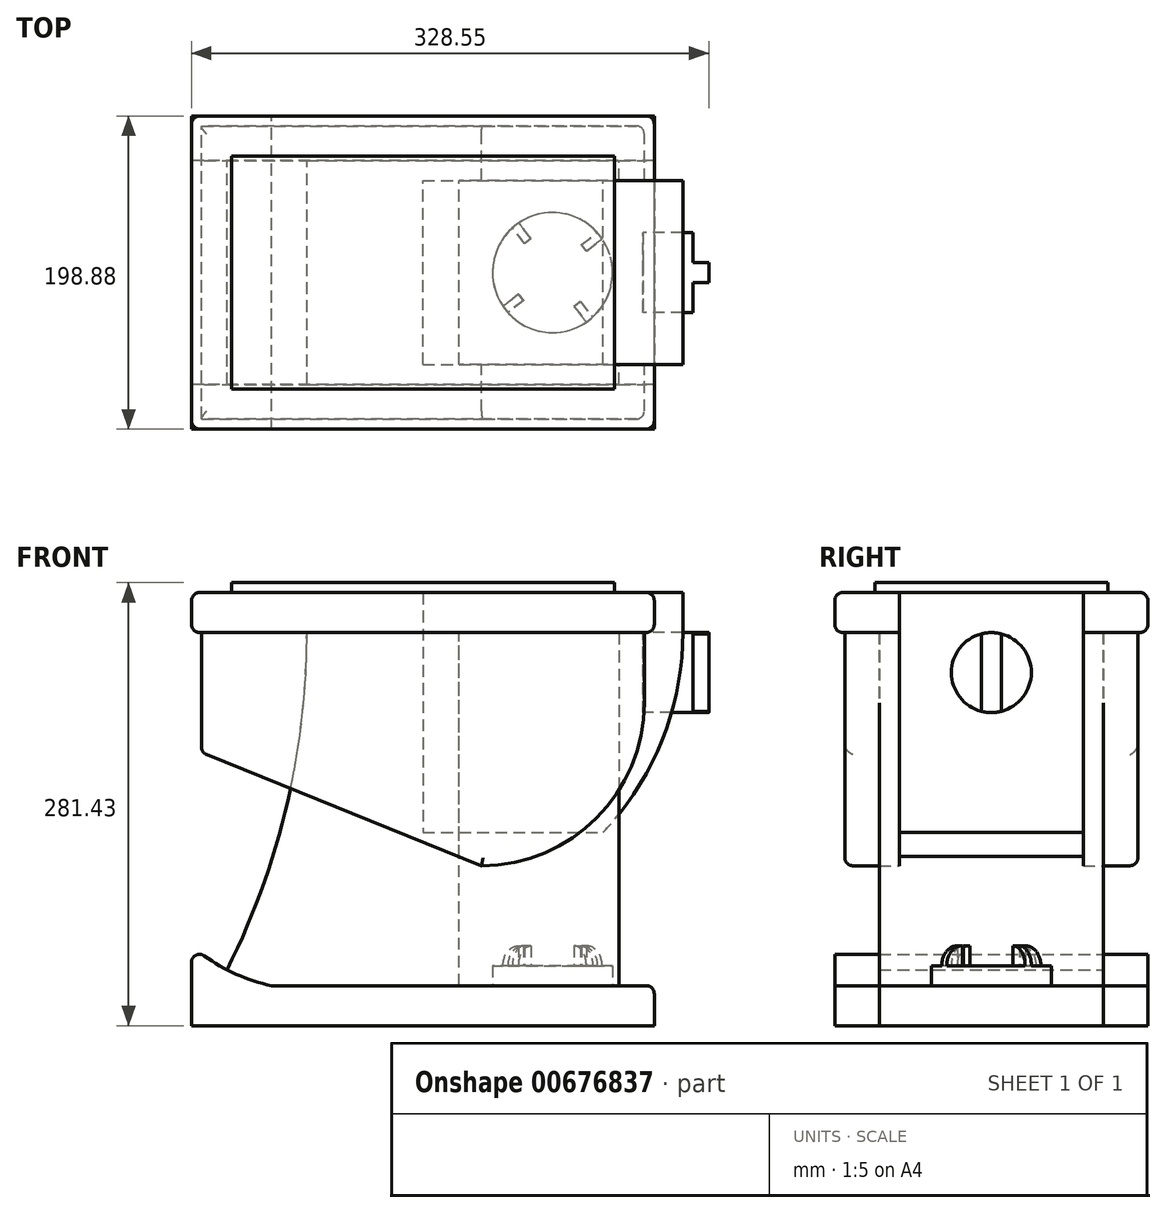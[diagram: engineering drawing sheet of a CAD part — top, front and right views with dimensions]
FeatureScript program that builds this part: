
annotation { "Feature Type Name" : "Feature", "Feature Type Description" : "" }
export const myFeature = defineFeature(function(context is Context, id is Id, definition is map)
    precondition{}
    {
        {
            var Q0;
            Q0=qCreatedBy(makeId("Top.planeOp"),FACE);
            var sketch = newSketch(context, id + "F0", { "sketchPlane" : qUnion([Q0])});
            skLineSegment(sketch, "E0.top", {"start": v(0, 99.44) * mm, "end": v(146.94, 99.44) * mm});
            skLineSegment(sketch, "E0.right", {"start": v(146.94, 0) * mm, "end": v(146.94, 99.44) * mm});
            skLineSegment(sketch, "E1.MirrorCS", {"start": v(0, 99.44) * mm, "end": v(-146.94, 99.44) * mm});
            skLineSegment(sketch, "E2.MirrorCS", {"start": v(-146.94, 0) * mm, "end": v(-146.94, 99.44) * mm});
            skLineSegment(sketch, "E3.MirrorCS", {"start": v(0, -99.44) * mm, "end": v(146.94, -99.44) * mm});
            skLineSegment(sketch, "E4.MirrorCS", {"start": v(146.94, 0) * mm, "end": v(146.94, -99.44) * mm});
            skLineSegment(sketch, "E5.MirrorCS", {"start": v(-146.94, 0) * mm, "end": v(-146.94, -99.44) * mm});
            skLineSegment(sketch, "E6.MirrorCS", {"start": v(0, -99.44) * mm, "end": v(-146.94, -99.44) * mm});
            skSolve(sketch);
        }
        {
            var Q0;
            Q0=qSketchRegion(id+"F0",true);
            extrude(context, id + "F1", {"entities" : qUnion([Q0]), "depth" : 25.4 * mm, "offsetDistance" : 25.4 * mm});
        }
        {
            var Q0;
            Q0=qCreatedBy(makeId("Front.planeOp"),FACE);
            var sketch = newSketch(context, id + "F2", { "sketchPlane" : qUnion([Q0])});
            skLineSegment(sketch, "E7.bottom", {"start": v(0, 0) * mm, "end": v(-140.59, 0) * mm});
            skLineSegment(sketch, "E7.top", {"start": v(0, -76.2) * mm, "end": v(-140.59, -76.2) * mm});
            skLineSegment(sketch, "E7.left", {"start": v(0, 0) * mm, "end": v(0, -76.2) * mm});
            skLineSegment(sketch, "E7.right", {"start": v(-140.59, 0) * mm, "end": v(-140.59, -76.2) * mm});
            skLineSegment(sketch, "E8.0", {"start": v(37.21, -148.08) * mm, "end": v(140.59, -148.08) * mm});
            skLineSegment(sketch, "E9", {"start": v(-140.59, -76.2) * mm, "end": v(37.21, -148.08) * mm});
            skLineSegment(sketch, "E10.0", {"start": v(140.59, 0) * mm, "end": v(140.59, -148.08) * mm});
            skLineSegment(sketch, "E11", {"start": v(0, 0) * mm, "end": v(140.59, 0) * mm});
            skSolve(sketch);
        }
        {
            var Q0;
            Q0=qSketchRegion(id+"F2",true);
            extrude(context, id + "F3", {"entities" : qUnion([Q0]), "operationType" : NewBodyOperationType.ADD, "depth" : 93.1 * mm, "offsetDistance" : 25.4 * mm, "hasSecondDirection" : true, "secondDirectionOppositeDirection" : true, "secondDirectionDepth" : 93.1 * mm});
        }
        {
            var Q0;
            Q0=qCreatedBy(makeId("Front.planeOp"),FACE);
            var sketch = newSketch(context, id + "F4", { "sketchPlane" : qUnion([Q0])});
            skLineSegment(sketch, "E12.bottom", {"start": v(0, 0) * mm, "end": v(124.46, 0) * mm});
            skLineSegment(sketch, "E12.top", {"start": v(0, -224.28) * mm, "end": v(124.46, -224.28) * mm});
            skLineSegment(sketch, "E12.left", {"start": v(0, 0) * mm, "end": v(0, -224.28) * mm});
            skLineSegment(sketch, "E12.right", {"start": v(124.46, 0) * mm, "end": v(124.46, -224.28) * mm});
            skLineSegment(sketch, "E13.MirrorCS", {"start": v(0, -224.28) * mm, "end": v(-96.14, -224.28) * mm});
            skLineSegment(sketch, "E14.bottom", {"start": v(0, -224.28) * mm, "end": v(146.94, -224.28) * mm});
            skLineSegment(sketch, "E14.top", {"start": v(0, -249.68) * mm, "end": v(146.94, -249.68) * mm});
            skLineSegment(sketch, "E14.right", {"start": v(146.94, -224.28) * mm, "end": v(146.94, -249.68) * mm});
            skLineSegment(sketch, "E15.MirrorCS", {"start": v(0, -249.68) * mm, "end": v(-146.94, -249.68) * mm});
            skLineSegment(sketch, "E16.MirrorCS", {"start": v(-146.94, -198.88) * mm, "end": v(-146.94, -249.68) * mm});
            skPoint(sketch, "E17.orphan", {"position": v(-146.94, -224.28) * mm});
            skArc(sketch, "E18", {"start": v(-146.94, -198.88) * mm, "mid": v(-123.18, -214.86) * mm, "end": v(-96.14, -224.28) * mm});
            skPoint(sketch, "E19.orphan", {"position": v(-124.46, -224.28) * mm});
            skLineSegment(sketch, "E20", {"start": v(-124.46, 0) * mm, "end": v(0, 0) * mm});
            skArc(sketch, "E21", {"start": v(-124.46, -214.2) * mm, "mid": v(-86.53, -110.07) * mm, "end": v(-73.66, 0) * mm});
            skSolve(sketch);
        }
        {
            var Q0;
            Q0=makeQuery(id+"F4.imprint","IMPRINT",FACE,{"disambiguationData":[TD([[makeQuery(id+"F4.imprint","IMPRINT",EDGE,{"derivedFrom":sQuery(id+"F4.wireOp",EDGE,"E14.top")}),1.0]])]});
            extrude(context, id + "F5", {"entities" : qUnion([Q0]), "depth" : 99.44 * mm, "offsetDistance" : 25.4 * mm, "hasSecondDirection" : true, "secondDirectionOppositeDirection" : true, "secondDirectionDepth" : 99.44 * mm});
        }
        {
            var Q0;
            Q0=qSketchRegion(id+"F4",true);
            extrude(context, id + "F6", {"entities" : qUnion([Q0]), "depth" : 71.12 * mm, "offsetDistance" : 25.4 * mm, "hasSecondDirection" : true, "secondDirectionOppositeDirection" : true, "secondDirectionDepth" : 71.12 * mm});
        }
        {
            var Q0;
            Q0=makeQuery(id+"F3.opExtrude","SWEPT_EDGE",EDGE,{"disambiguationData":[OSD([sQuery(id+"F2.wireOp",EDGE,"E8.0"),sQuery(id+"F2.wireOp",EDGE,"E10.0")])]});
            fillet(context, id + "F7", {"entities" : qUnion([Q0]), "radius" : 103.38 * mm, "tangentPropagation" : true, "allowEdgeOverflow" : false});
        }
        {
            var Q0;
            Q0=makeQuery(id+"F6.opExtrude","SWEPT_FACE",FACE,{"disambiguationData":[OSD([sQuery(id+"F4.wireOp",EDGE,"E12.right")])]});
            var sketch = newSketch(context, id + "F8", { "sketchPlane" : qUnion([Q0])});
            skLineSegment(sketch, "E22.0", {"start": v(-58.42, -224.28) * mm, "end": v(-58.42, -49.7) * mm});
            skLineSegment(sketch, "E23.bottom", {"start": v(-58.42, -224.28) * mm, "end": v(58.42, -224.28) * mm});
            skLineSegment(sketch, "E23.top", {"start": v(-58.42, 0) * mm, "end": v(58.42, 0) * mm});
            skLineSegment(sketch, "E23.left", {"start": v(-58.42, -224.28) * mm, "end": v(-58.42, 0) * mm});
            skLineSegment(sketch, "E23.right", {"start": v(58.42, -224.28) * mm, "end": v(58.42, 0) * mm});
            skSolve(sketch);
        }
        {
            var Q0;
            Q0=makeQuery(id+"F1.opExtrude","CAP_FACE",FACE,{"disambiguationData":[OSD([sQuery(id+"F0.wireOp",EDGE,"E0.top"),sQuery(id+"F0.wireOp",EDGE,"E0.right"),sQuery(id+"F0.wireOp",EDGE,"E1.MirrorCS"),sQuery(id+"F0.wireOp",EDGE,"E2.MirrorCS"),sQuery(id+"F0.wireOp",EDGE,"E3.MirrorCS"),sQuery(id+"F0.wireOp",EDGE,"E4.MirrorCS"),sQuery(id+"F0.wireOp",EDGE,"E5.MirrorCS"),sQuery(id+"F0.wireOp",EDGE,"E6.MirrorCS")])],"isStart":false});
            var Q1;
            Q1=makeQuery(id+"F1.opExtrude","CAP_EDGE",EDGE,{"disambiguationData":[OSD([sQuery(id+"F0.wireOp",EDGE,"E3.MirrorCS"),sQuery(id+"F0.wireOp",EDGE,"E6.MirrorCS")])],"isStart":true});
            var Q2;
            Q2=makeQuery(id+"F1.opExtrude","CAP_EDGE",EDGE,{"disambiguationData":[OSD([sQuery(id+"F0.wireOp",EDGE,"E2.MirrorCS"),sQuery(id+"F0.wireOp",EDGE,"E5.MirrorCS")])],"isStart":true});
            var Q3;
            Q3=makeQuery(id+"F1.opExtrude","SWEPT_FACE",FACE,{"disambiguationData":[OSD([sQuery(id+"F0.wireOp",EDGE,"E0.right"),sQuery(id+"F0.wireOp",EDGE,"E4.MirrorCS")])]});
            var Q4;
            Q4=makeQuery(id+"F1.opExtrude","SWEPT_FACE",FACE,{"disambiguationData":[OSD([sQuery(id+"F0.wireOp",EDGE,"E2.MirrorCS"),sQuery(id+"F0.wireOp",EDGE,"E5.MirrorCS")])]});
            var Q5;
            Q5=makeQuery(id+"F1.opExtrude","SWEPT_FACE",FACE,{"disambiguationData":[OSD([sQuery(id+"F0.wireOp",EDGE,"E0.top"),sQuery(id+"F0.wireOp",EDGE,"E1.MirrorCS")])]});
            fillet(context, id + "F9", {"entities" : qUnion([Q0, Q1, Q2, Q3, Q4, Q5]), "radius" : 5.08 * mm, "tangentPropagation" : true, "allowEdgeOverflow" : false});
        }
        {
            var Q0;
            Q0=makeQuery(id+"F3.opExtrude","SWEPT_EDGE",EDGE,{"disambiguationData":[OSD([sQuery(id+"F2.wireOp",EDGE,"E7.top"),sQuery(id+"F2.wireOp",EDGE,"E7.right"),sQuery(id+"F2.wireOp",EDGE,"E9")])]});
            var Q1;
            Q1=makeQuery(id+"F3.opExtrude","CAP_EDGE",EDGE,{"disambiguationData":[OSD([sQuery(id+"F2.wireOp",EDGE,"E9")])],"isStart":false});
            var Q2;
            Q2=makeQuery(id+"F3.opExtrude","CAP_EDGE",EDGE,{"disambiguationData":[OSD([sQuery(id+"F2.wireOp",EDGE,"E9")])],"isStart":true});
            var Q3;
            {var subQ0=sQuery(id+"F2.wireOp",EDGE,"E10.0");var subQ1=sQuery(id+"F2.wireOp",EDGE,"E8.0");Q3=makeQuery(id+"F7.opFillet","BLEND_EDGE",EDGE,{"blendedFrom":[makeQuery(id+"F3.opExtrude","SWEPT_EDGE",EDGE,{"disambiguationData":[OSD([subQ1,subQ0])]}),makeQuery(id+"F3.opExtrude","CAP_FACE",FACE,{"disambiguationData":[OSD([sQuery(id+"F2.wireOp",EDGE,"E7.bottom"),sQuery(id+"F2.wireOp",EDGE,"E7.right"),subQ1,sQuery(id+"F2.wireOp",EDGE,"E9"),subQ0,sQuery(id+"F2.wireOp",EDGE,"E11")])],"isStart":true})],"blendedInto":[makeQuery(id+"F3.opExtrude","CAP_FACE",FACE,{"disambiguationData":[OSD([sQuery(id+"F2.wireOp",EDGE,"E7.bottom"),sQuery(id+"F2.wireOp",EDGE,"E7.right"),subQ1,sQuery(id+"F2.wireOp",EDGE,"E9"),subQ0,sQuery(id+"F2.wireOp",EDGE,"E11")])],"isStart":true})]});}
            var Q4;
            {var subQ0=sQuery(id+"F2.wireOp",EDGE,"E10.0");var subQ1=sQuery(id+"F2.wireOp",EDGE,"E8.0");Q4=makeQuery(id+"F7.opFillet","BLEND_EDGE",EDGE,{"blendedFrom":[makeQuery(id+"F3.opExtrude","SWEPT_EDGE",EDGE,{"disambiguationData":[OSD([subQ1,subQ0])]}),makeQuery(id+"F3.opExtrude","CAP_FACE",FACE,{"disambiguationData":[OSD([sQuery(id+"F2.wireOp",EDGE,"E7.bottom"),sQuery(id+"F2.wireOp",EDGE,"E7.right"),subQ1,sQuery(id+"F2.wireOp",EDGE,"E9"),subQ0,sQuery(id+"F2.wireOp",EDGE,"E11")])],"isStart":false})],"blendedInto":[makeQuery(id+"F3.opExtrude","CAP_FACE",FACE,{"disambiguationData":[OSD([sQuery(id+"F2.wireOp",EDGE,"E7.bottom"),sQuery(id+"F2.wireOp",EDGE,"E7.right"),subQ1,sQuery(id+"F2.wireOp",EDGE,"E9"),subQ0,sQuery(id+"F2.wireOp",EDGE,"E11")])],"isStart":false})]});}
            var Q5;
            Q5=makeQuery(id+"F5.opExtrude","SWEPT_EDGE",EDGE,{"disambiguationData":[OSD([sQuery(id+"F4.wireOp",EDGE,"E16.MirrorCS"),sQuery(id+"F4.wireOp",EDGE,"E18")])]});
            var Q6;
            Q6=makeQuery(id+"F6.opExtrude","SWEPT_EDGE",EDGE,{"disambiguationData":[OSD([sQuery(id+"F4.wireOp",EDGE,"E16.MirrorCS"),sQuery(id+"F4.wireOp",EDGE,"E18")])]});
            var Q7;
            Q7=makeQuery(id+"F6.opExtrude","SWEPT_EDGE",EDGE,{"disambiguationData":[OSD([sQuery(id+"F4.wireOp",EDGE,"E14.bottom"),sQuery(id+"F4.wireOp",EDGE,"E14.right")])]});
            var Q8;
            Q8=makeQuery(id+"F5.opExtrude","SWEPT_EDGE",EDGE,{"disambiguationData":[OSD([sQuery(id+"F4.wireOp",EDGE,"E14.bottom"),sQuery(id+"F4.wireOp",EDGE,"E14.right")])]});
            fillet(context, id + "F10", {"entities" : qUnion([Q0, Q1, Q2, Q3, Q4, Q5, Q6, Q7, Q8]), "radius" : 5.08 * mm, "tangentPropagation" : true, "allowEdgeOverflow" : false});
        }
        {
            var Q0;
            Q0=makeQuery(id+"F1.opExtrude","CAP_FACE",FACE,{"disambiguationData":[OSD([sQuery(id+"F0.wireOp",EDGE,"E0.top"),sQuery(id+"F0.wireOp",EDGE,"E0.right"),sQuery(id+"F0.wireOp",EDGE,"E1.MirrorCS"),sQuery(id+"F0.wireOp",EDGE,"E2.MirrorCS"),sQuery(id+"F0.wireOp",EDGE,"E3.MirrorCS"),sQuery(id+"F0.wireOp",EDGE,"E4.MirrorCS"),sQuery(id+"F0.wireOp",EDGE,"E5.MirrorCS"),sQuery(id+"F0.wireOp",EDGE,"E6.MirrorCS")])],"isStart":false});
            var sketch = newSketch(context, id + "F11", { "sketchPlane" : qUnion([Q0])});
            skLineSegment(sketch, "E24.bottom", {"start": v(121.54, 74.04) * mm, "end": v(-121.54, 74.04) * mm});
            skLineSegment(sketch, "E24.top", {"start": v(121.54, -74.04) * mm, "end": v(-121.54, -74.04) * mm});
            skLineSegment(sketch, "E24.left", {"start": v(121.54, 74.04) * mm, "end": v(121.54, -74.04) * mm});
            skLineSegment(sketch, "E24.right", {"start": v(-121.54, 74.04) * mm, "end": v(-121.54, -74.04) * mm});
            skPoint(sketch, "E24.middle", {"position": v(0, 0) * mm});
            skSolve(sketch);
        }
        {
            var Q0;
            Q0=qSketchRegion(id+"F11",true);
            extrude(context, id + "F12", {"entities" : qUnion([Q0]), "operationType" : NewBodyOperationType.ADD, "depth" : 6.35 * mm, "offsetDistance" : 25.4 * mm});
        }
        {
            var Q0;
            {var subQ4=sQuery(id+"F8.wireOp",EDGE,"E23.bottom");Q0=makeQuery(id+"F8.imprint","IMPRINT",FACE,{"disambiguationData":[TD([[makeQuery(id+"F8.imprint","IMPRINT",EDGE,{"derivedFrom":subQ4}),1.0]])]});}
            extrude(context, id + "F13", {"entities" : qUnion([Q0]), "operationType" : NewBodyOperationType.REMOVE, "oppositeDirection" : true, "depth" : 101.6 * mm, "offsetDistance" : 25.4 * mm, "hasSecondDirection" : true, "secondDirectionOppositeDirection" : false, "secondDirectionDepth" : 25.4 * mm});
        }
        {
            var Q0;
            Q0=qCreatedBy(makeId("Front.planeOp"),FACE);
            var sketch = newSketch(context, id + "F14", { "sketchPlane" : qUnion([Q0])});
            skLineSegment(sketch, "E25.bottom", {"start": v(0, 0) * mm, "end": v(165.1, 0) * mm});
            skLineSegment(sketch, "E25.top", {"start": v(0, -127) * mm, "end": v(114.3, -127) * mm});
            skLineSegment(sketch, "E25.left", {"start": v(0, 0) * mm, "end": v(0, -127) * mm});
            skLineSegment(sketch, "E26.top", {"start": v(0, 25.4) * mm, "end": v(165.1, 25.4) * mm});
            skLineSegment(sketch, "E26.left", {"start": v(0, 0) * mm, "end": v(0, 25.4) * mm});
            skLineSegment(sketch, "E26.right", {"start": v(165.1, 0) * mm, "end": v(165.1, 25.4) * mm});
            skArc(sketch, "E27", {"start": v(114.3, -127) * mm, "mid": v(151.93, -68.4) * mm, "end": v(165.1, 0) * mm});
            skSolve(sketch);
        }
        {
            var Q0;
            Q0=qSketchRegion(id+"F14",true);
            extrude(context, id + "F15", {"entities" : qUnion([Q0]), "depth" : 58.42 * mm, "offsetDistance" : 25.4 * mm, "hasSecondDirection" : true, "secondDirectionOppositeDirection" : true, "secondDirectionDepth" : 58.42 * mm});
        }
        {
            var Q0;
            Q0=makeQuery(id+"F15.opExtrude","SWEPT_FACE",FACE,{"disambiguationData":[OSD([sQuery(id+"F14.wireOp",EDGE,"E26.right")])]});
            var sketch = newSketch(context, id + "F16", { "sketchPlane" : qUnion([Q0])});
            skLineSegment(sketch, "E28", {"start": v(0, 25.4) * mm, "end": v(0, -81.4) * mm});
            skLineSegment(sketch, "E29", {"start": v(0, 25.4) * mm, "end": v(34.21, 25.4) * mm});
            skLineSegment(sketch, "E30.0", {"start": v(0, -25.4) * mm, "end": v(34.21, -25.4) * mm});
            skCircle(sketch, "E31", {"center": v(0, -25.4) * mm, "radius": 25.4 * mm});
            skSolve(sketch);
        }
        {
            var Q0;
            Q0=qSketchRegion(id+"F16",true);
            extrude(context, id + "F17", {"entities" : qUnion([Q0]), "depth" : 6.35 * mm, "offsetDistance" : 25.4 * mm, "hasSecondDirection" : true, "secondDirectionOppositeDirection" : true, "secondDirectionDepth" : 25.4 * mm});
        }
        {
            var Q0;
            Q0=makeQuery(id+"F17.opExtrude","CAP_FACE",FACE,{"disambiguationData":[OSD([sQuery(id+"F16.wireOp",EDGE,"E31")])],"isStart":false});
            var sketch = newSketch(context, id + "F18", { "sketchPlane" : qUnion([Q0])});
            skArc(sketch, "E32", {"start": v(-6.35, -50) * mm, "mid": v(0, -50.8) * mm, "end": v(6.35, -50) * mm});
            skLineSegment(sketch, "E33.0", {"start": v(-6.35, -0.8) * mm, "end": v(-6.35, -50) * mm});
            skLineSegment(sketch, "E34.0", {"start": v(6.35, -0.8) * mm, "end": v(6.35, -50) * mm});
            skArc(sketch, "E35.trimOffspring", {"start": v(6.35, -0.8) * mm, "mid": v(0, 0) * mm, "end": v(-6.35, -0.8) * mm});
            skSolve(sketch);
        }
        {
            var Q0;
            Q0=makeQuery(id+"F18.imprint","IMPRINT",FACE,{"disambiguationData":[TD([[makeQuery(id+"F18.imprint","IMPRINT",EDGE,{"derivedFrom":sQuery(id+"F18.wireOp",EDGE,"E32")}),1.0]])]});
            extrude(context, id + "F19", {"entities" : qUnion([Q0]), "operationType" : NewBodyOperationType.ADD, "depth" : 10.16 * mm, "offsetDistance" : 25.4 * mm});
        }
        {
            var Q0;
            Q0=makeQuery(id+"F13.boolean.opBoolean","MERGE",FACE,{"derivedFrom":[makeQuery(id+"F6.opExtrude","SWEPT_FACE",FACE,{"disambiguationData":[OSD([sQuery(id+"F4.wireOp",EDGE,"E14.bottom")])]}),makeQuery(id+"F13.opExtrude","SWEPT_FACE",FACE,{"disambiguationData":[OSD([sQuery(id+"F8.wireOp",EDGE,"E23.bottom")])]})]});
            var sketch = newSketch(context, id + "F20", { "sketchPlane" : qUnion([Q0])});
            skLineSegment(sketch, "E36", {"start": v(22.86, 0) * mm, "end": v(141.86, 0) * mm});
            skCircle(sketch, "E37", {"center": v(82.36, 0) * mm, "radius": 38.1 * mm});
            skSolve(sketch);
        }
        {
            var Q0;
            Q0=qSketchRegion(id+"F20",true);
            extrude(context, id + "F21", {"entities" : qUnion([Q0]), "depth" : 12.7 * mm, "offsetDistance" : 25.4 * mm});
        }
        {
            var Q0;
            Q0=makeQuery(id+"F21.opExtrude","CAP_FACE",FACE,{"disambiguationData":[OSD([sQuery(id+"F20.wireOp",EDGE,"E37")])],"isStart":false});
            var sketch = newSketch(context, id + "F22", { "sketchPlane" : qUnion([Q0])});
            skArc(sketch, "E38", {"start": v(103.8, -31.5) * mm, "mid": v(105.86, -30) * mm, "end": v(107.8, -28.36) * mm});
            skLineSegment(sketch, "E39.0", {"start": v(103.92, 13.67) * mm, "end": v(100.79, 17.66) * mm});
            skLineSegment(sketch, "E40.0", {"start": v(63.93, -17.66) * mm, "end": v(60.8, -13.67) * mm});
            skLineSegment(sketch, "E41.0", {"start": v(100.02, -18.43) * mm, "end": v(96.02, -21.56) * mm});
            skLineSegment(sketch, "E42.0", {"start": v(68.7, 21.56) * mm, "end": v(64.7, 18.43) * mm});
            skArc(sketch, "E43.trimOffspring", {"start": v(113.85, 21.45) * mm, "mid": v(112.35, 23.5) * mm, "end": v(110.72, 25.44) * mm});
            skArc(sketch, "E44.trimOffspring", {"start": v(60.91, 31.5) * mm, "mid": v(58.86, 30) * mm, "end": v(56.92, 28.36) * mm});
            skArc(sketch, "E45.trimOffspring", {"start": v(50.87, -21.45) * mm, "mid": v(52.37, -23.5) * mm, "end": v(54, -25.44) * mm});
            skLineSegment(sketch, "E46.trimOffspring", {"start": v(64.7, 18.43) * mm, "end": v(56.92, 28.36) * mm});
            skLineSegment(sketch, "E47.trimOffspring", {"start": v(100.79, 17.66) * mm, "end": v(110.78, 25.5) * mm});
            skLineSegment(sketch, "E48.trimOffspring", {"start": v(103.92, 13.67) * mm, "end": v(113.92, 21.5) * mm});
            skLineSegment(sketch, "E49.trimOffspring", {"start": v(68.7, 21.56) * mm, "end": v(60.91, 31.5) * mm});
            skLineSegment(sketch, "E50.trimOffspring", {"start": v(96.02, -21.56) * mm, "end": v(103.8, -31.5) * mm});
            skLineSegment(sketch, "E51.trimOffspring", {"start": v(63.93, -17.66) * mm, "end": v(54, -25.44) * mm});
            skLineSegment(sketch, "E52.trimOffspring", {"start": v(60.8, -13.67) * mm, "end": v(50.87, -21.45) * mm});
            skLineSegment(sketch, "E53.trimOffspring", {"start": v(100.02, -18.43) * mm, "end": v(107.8, -28.36) * mm});
            skSolve(sketch);
        }
        {
            var Q0;
            Q0=qSketchRegion(id+"F22",true);
            extrude(context, id + "F23", {"entities" : qUnion([Q0]), "operationType" : NewBodyOperationType.ADD, "depth" : 12.7 * mm, "offsetDistance" : 25.4 * mm});
        }
        {
            var Q0;
            Q0=makeQuery(id+"F23.opExtrude","CAP_EDGE",EDGE,{"disambiguationData":[OSD([sQuery(id+"F22.wireOp",EDGE,"E43.trimOffspring")])],"isStart":false});
            var Q1;
            Q1=makeQuery(id+"F23.opExtrude","CAP_EDGE",EDGE,{"disambiguationData":[OSD([sQuery(id+"F22.wireOp",EDGE,"E44.trimOffspring")])],"isStart":false});
            var Q2;
            Q2=makeQuery(id+"F23.opExtrude","CAP_EDGE",EDGE,{"disambiguationData":[OSD([sQuery(id+"F22.wireOp",EDGE,"E38")])],"isStart":false});
            var Q3;
            Q3=makeQuery(id+"F23.opExtrude","CAP_EDGE",EDGE,{"disambiguationData":[OSD([sQuery(id+"F22.wireOp",EDGE,"E45.trimOffspring")])],"isStart":false});
            fillet(context, id + "F24", {"entities" : qUnion([Q0, Q1, Q2, Q3]), "radius" : 12.7 * mm, "tangentPropagation" : true, "allowEdgeOverflow" : false});
        }
    });
